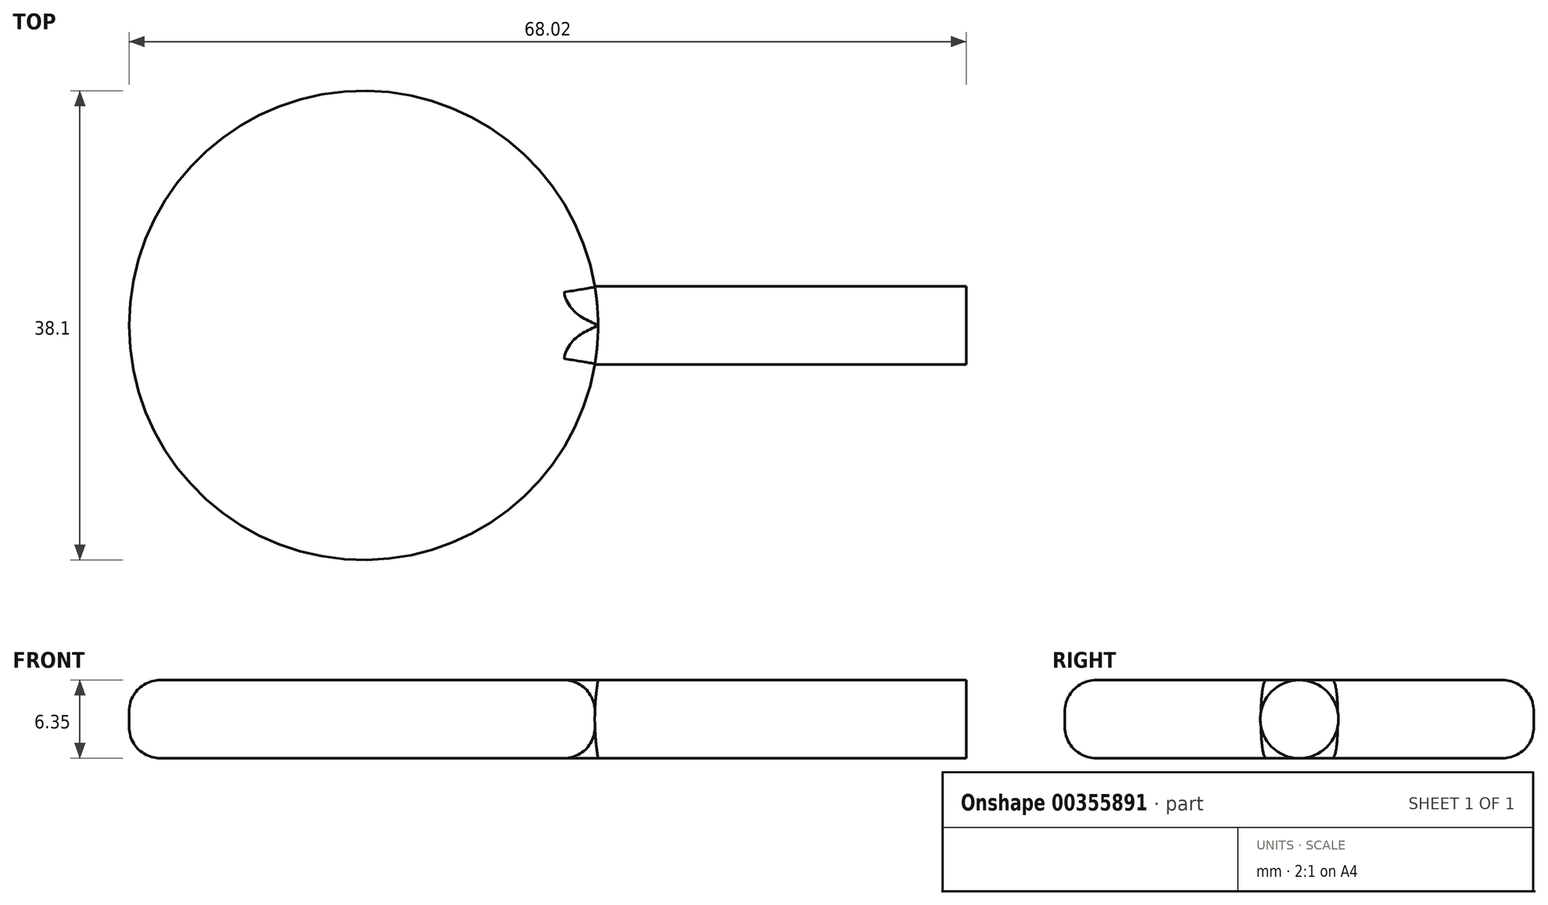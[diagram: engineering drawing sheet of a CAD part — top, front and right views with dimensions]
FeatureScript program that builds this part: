
annotation { "Feature Type Name" : "Feature", "Feature Type Description" : "" }
export const myFeature = defineFeature(function(context is Context, id is Id, definition is map)
    precondition{}
    {
        {
            var Q0;
            Q0=qCreatedBy(makeId("Top.planeOp"),FACE);
            var sketch = newSketch(context, id + "F0", { "sketchPlane" : qUnion([Q0])});
            skCircle(sketch, "E0", {"center": v(0, 0) * mm, "radius": 19.05 * mm});
            skLineSegment(sketch, "E1.bottom", {"start": v(48.97, -3.17) * mm, "end": v(18.78, -3.17) * mm});
            skLineSegment(sketch, "E1.top", {"start": v(48.97, 3.18) * mm, "end": v(18.78, 3.18) * mm});
            skLineSegment(sketch, "E1.left", {"start": v(48.97, -3.17) * mm, "end": v(48.97, 3.18) * mm});
            skPoint(sketch, "E1.right.end.orphan", {"position": v(-48.97, 3.17) * mm});
            skPoint(sketch, "E1.right.start.orphan", {"position": v(-48.97, -3.18) * mm});
            skSolve(sketch);
        }
        {
            var Q0;
            Q0=qSketchRegion(id+"F0",true);
            extrude(context, id + "F1", {"entities" : qUnion([Q0]), "depth" : 6.35 * mm});
        }
        {
            var Q0;
            Q0=makeQuery(id+"F1.opExtrude","CAP_EDGE",EDGE,{"disambiguationData":[OSD([sQuery(id+"F0.wireOp",EDGE,"E1.bottom")])],"isStart":false});
            var Q1;
            Q1=makeQuery(id+"F1.opExtrude","CAP_EDGE",EDGE,{"disambiguationData":[OSD([sQuery(id+"F0.wireOp",EDGE,"E1.top")])],"isStart":false});
            var Q2;
            Q2=makeQuery(id+"F1.opExtrude","CAP_EDGE",EDGE,{"disambiguationData":[OSD([sQuery(id+"F0.wireOp",EDGE,"E1.bottom")])],"isStart":true});
            var Q3;
            Q3=makeQuery(id+"F1.opExtrude","CAP_EDGE",EDGE,{"disambiguationData":[OSD([sQuery(id+"F0.wireOp",EDGE,"E1.top")])],"isStart":true});
            fillet(context, id + "F2", {"entities" : qUnion([Q0, Q1, Q2, Q3]), "radius" : 3.17 * mm, "tangentPropagation" : true, "allowEdgeOverflow" : false});
        }
        {
            var Q0;
            Q0=makeQuery(id+"F1.opExtrude","CAP_EDGE",EDGE,{"disambiguationData":[OSD([sQuery(id+"F0.wireOp",EDGE,"E0")])],"isStart":true});
            var Q1;
            Q1=makeQuery(id+"F1.opExtrude","CAP_FACE",FACE,{"disambiguationData":[OSD([sQuery(id+"F0.wireOp",EDGE,"E0"),sQuery(id+"F0.wireOp",EDGE,"E1.bottom"),sQuery(id+"F0.wireOp",EDGE,"E1.top"),sQuery(id+"F0.wireOp",EDGE,"E1.left")])],"isStart":false});
            fillet(context, id + "F3", {"entities" : qUnion([Q0, Q1]), "radius" : 2.54 * mm, "tangentPropagation" : true, "allowEdgeOverflow" : false});
        }
    });
